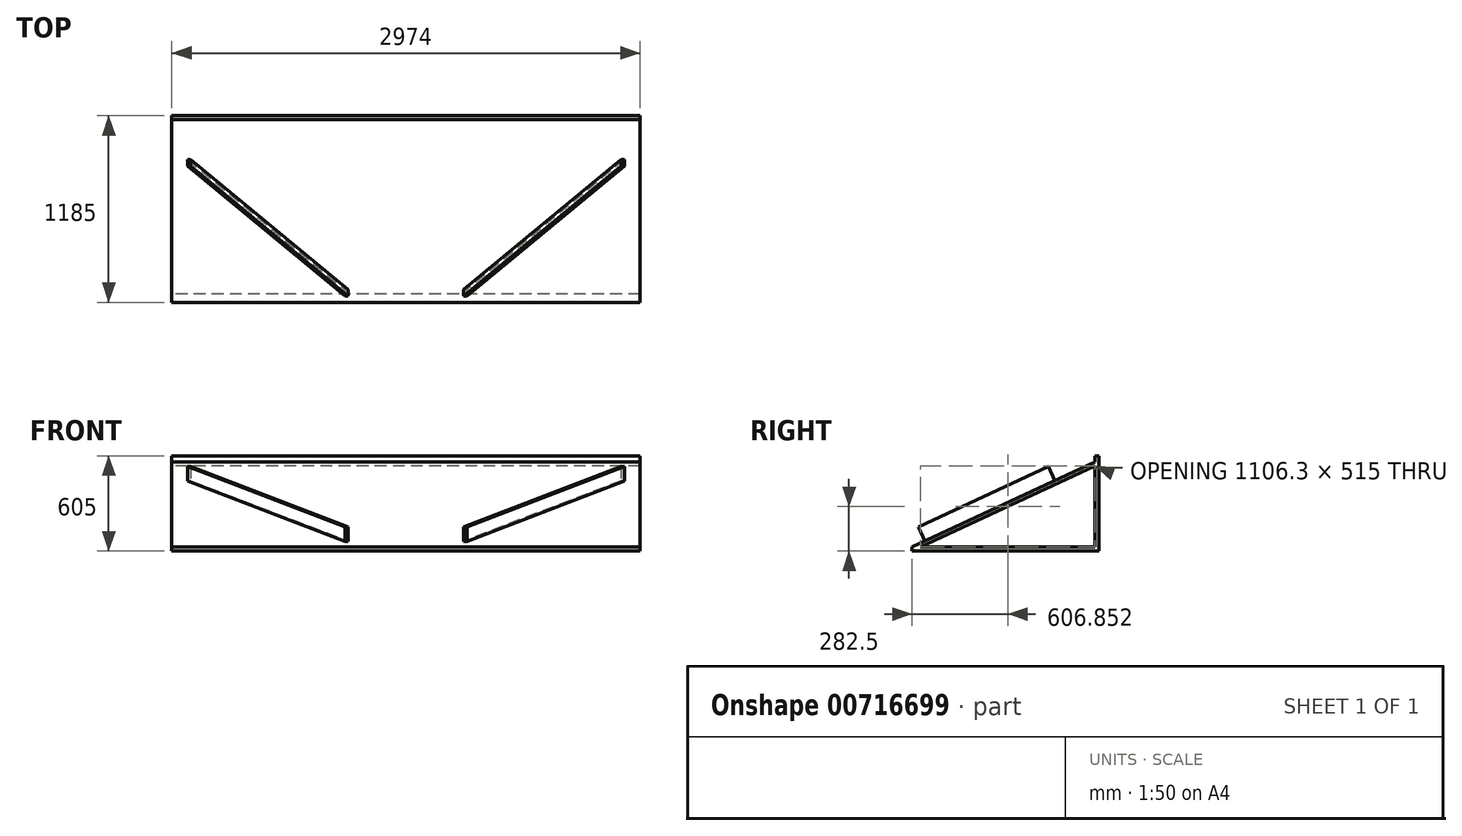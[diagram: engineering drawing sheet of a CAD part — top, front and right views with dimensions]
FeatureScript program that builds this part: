
annotation { "Feature Type Name" : "Feature", "Feature Type Description" : "" }
export const myFeature = defineFeature(function(context is Context, id is Id, definition is map)
    precondition{}
    {
        {
            var Q0;
            Q0=qCreatedBy(makeId("Right.planeOp"),FACE);
            cPlane(context, id + "F0", {"entities" : qUnion([Q0]), "cplaneType" : CPlaneType.OFFSET, "offset" : (2974 / 2) * mm, "width" : 150 * mm, "height" : 150 * mm});
        }
        {
            var Q0;
            Q0=qCreatedBy(makeId("Top.planeOp"),FACE);
            var sketch = newSketch(context, id + "F1", { "sketchPlane" : qUnion([Q0])});
            skLineSegment(sketch, "E0.bottom", {"start": v(0, 0) * mm, "end": v(2974, 0) * mm});
            skLineSegment(sketch, "E0.top", {"start": v(0, 1185) * mm, "end": v(2974, 1185) * mm});
            skLineSegment(sketch, "E0.left", {"start": v(0, 0) * mm, "end": v(0, 1185) * mm});
            skLineSegment(sketch, "E0.right", {"start": v(2974, 0) * mm, "end": v(2974, 1185) * mm});
            skSolve(sketch);
        }
        {
            var Q0;
            Q0=makeQuery(id+"F1.imprint","IMPRINT",FACE,{"disambiguationData":[TD([[makeQuery(id+"F1.imprint","IMPRINT",EDGE,{"derivedFrom":sQuery(id+"F1.wireOp",EDGE,"E0.bottom")}),1.0]])]});
            extrude(context, id + "F2", {"entities" : qUnion([Q0]), "depth" : 25 * mm, "offsetDistance" : 25 * mm});
        }
        {
            var Q0;
            Q0=makeQuery(id+"F2.opExtrude","CAP_FACE",FACE,{"disambiguationData":[OSD([sQuery(id+"F1.wireOp",EDGE,"E0.bottom"),sQuery(id+"F1.wireOp",EDGE,"E0.top"),sQuery(id+"F1.wireOp",EDGE,"E0.left"),sQuery(id+"F1.wireOp",EDGE,"E0.right")])],"isStart":false});
            var sketch = newSketch(context, id + "F3", { "sketchPlane" : qUnion([Q0])});
            skLineSegment(sketch, "E1.bottom", {"start": v(0, 1185) * mm, "end": v(2974, 1185) * mm});
            skLineSegment(sketch, "E1.top", {"start": v(0, 1160) * mm, "end": v(2974, 1160) * mm});
            skLineSegment(sketch, "E1.left", {"start": v(0, 1185) * mm, "end": v(0, 1160) * mm});
            skLineSegment(sketch, "E1.right", {"start": v(2974, 1185) * mm, "end": v(2974, 1160) * mm});
            skSolve(sketch);
        }
        {
            var Q0;
            Q0 = qSketchRegion(id + "F3", true);
            extrude(context, id + "F4", {"entities" : qUnion([Q0]), "operationType" : NewBodyOperationType.ADD, "depth" : 580 * mm, "offsetDistance" : 25 * mm});
        }
        {
            var Q0;
            Q0=qCreatedBy(makeId("Right.planeOp"),FACE);
            var sketch = newSketch(context, id + "F5", { "sketchPlane" : qUnion([Q0])});
            skLineSegment(sketch, "E2.0", {"start": v(1160, 605) * mm, "end": v(1160, 25) * mm});
            skLineSegment(sketch, "E3", {"start": v(1160, 565) * mm, "end": v(0, 25) * mm});
            skLineSegment(sketch, "E4.0", {"start": v(0, 25) * mm, "end": v(1160, 25) * mm});
            skLineSegment(sketch, "E5", {"start": v(1160, 540) * mm, "end": v(53.7, 25) * mm});
            skSolve(sketch);
        }
        {
            var Q0;
            {var subQ0=sQuery(id+"F5.wireOp",EDGE,"E3");Q0=makeQuery(id+"F5.imprint","IMPRINT",FACE,{"disambiguationData":[TD([[makeQuery(id+"F5.imprint","IMPRINT",EDGE,{"derivedFrom":subQ0}),1.0]])]});}
            extrude(context, id + "F6", {"entities" : qUnion([Q0]), "operationType" : NewBodyOperationType.ADD, "depth" : 2974 * mm, "offsetDistance" : 25 * mm});
        }
        {
            var Q0;
            Q0=makeQuery(id+"F6.opExtrude","SWEPT_FACE",FACE,{"disambiguationData":[OSD([sQuery(id+"F5.wireOp",EDGE,"E3")])]});
            var sketch = newSketch(context, id + "F7", { "sketchPlane" : qUnion([Q0])});
            skLineSegment(sketch, "E6", {"start": v(100, 1010.55) * mm, "end": v(1100, 100) * mm});
            skLineSegment(sketch, "E7", {"start": v(100, 1010.55) * mm, "end": v(120, 1010.55) * mm});
            skLineSegment(sketch, "E8", {"start": v(120, 1010.55) * mm, "end": v(1120, 100) * mm});
            skLineSegment(sketch, "E9", {"start": v(1100, 100) * mm, "end": v(1120, 100) * mm});
            skLineSegment(sketch, "E10.MirrorCS", {"start": v(2874, 1010.55) * mm, "end": v(2854, 1010.55) * mm});
            skLineSegment(sketch, "E11.MirrorCS", {"start": v(1874, 100) * mm, "end": v(1854, 100) * mm});
            skLineSegment(sketch, "E12.MirrorCS", {"start": v(2854, 1010.55) * mm, "end": v(1854, 100) * mm});
            skLineSegment(sketch, "E13.MirrorCS", {"start": v(2874, 1010.55) * mm, "end": v(1874, 100) * mm});
            skSolve(sketch);
        }
        {
            var Q0;
            Q0 = qSketchRegion(id + "F7", true);
            extrude(context, id + "F8", {"entities" : qUnion([Q0]), "operationType" : NewBodyOperationType.ADD, "depth" : 100 * mm, "offsetDistance" : 25 * mm});
        }
    });
